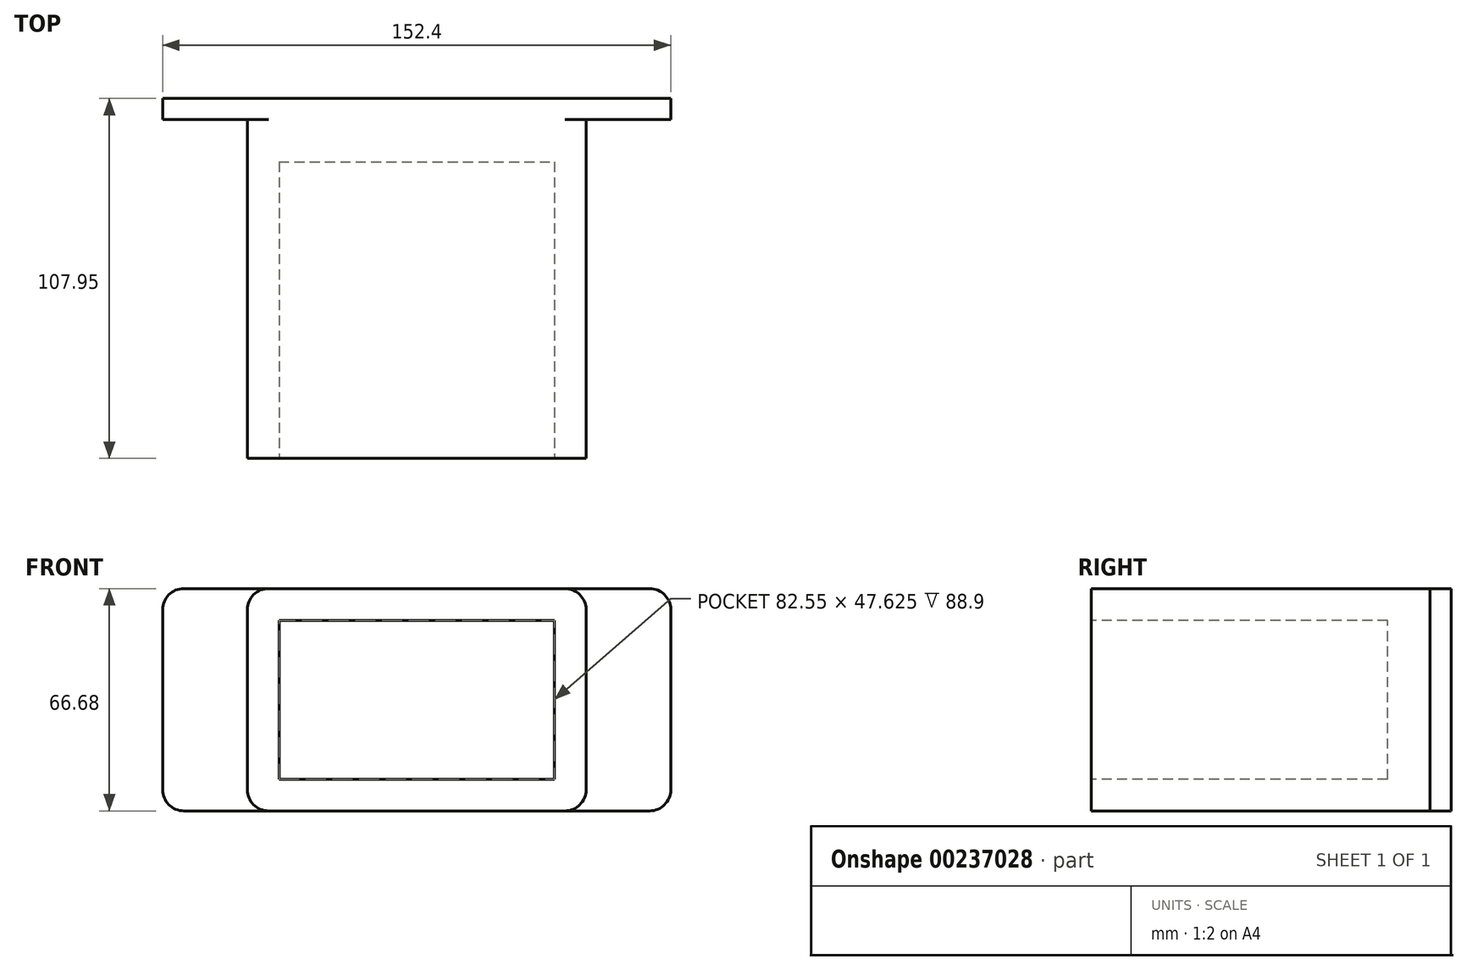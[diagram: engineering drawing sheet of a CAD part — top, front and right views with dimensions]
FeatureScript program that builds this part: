
annotation { "Feature Type Name" : "Feature", "Feature Type Description" : "" }
export const myFeature = defineFeature(function(context is Context, id is Id, definition is map)
    precondition{}
    {
        {
            var Q0;
            Q0=qCreatedBy(makeId("Front.planeOp"),FACE);
            var sketch = newSketch(context, id + "F0", { "sketchPlane" : qUnion([Q0])});
            skLineSegment(sketch, "E0.bottom", {"start": v(-76.2, -33.34) * mm, "end": v(76.2, -33.34) * mm});
            skLineSegment(sketch, "E0.top", {"start": v(-76.2, 33.34) * mm, "end": v(76.2, 33.34) * mm});
            skLineSegment(sketch, "E0.left", {"start": v(-76.2, -33.34) * mm, "end": v(-76.2, 33.34) * mm});
            skLineSegment(sketch, "E0.right", {"start": v(76.2, -33.34) * mm, "end": v(76.2, 33.34) * mm});
            skPoint(sketch, "E0.middle", {"position": v(0, 0) * mm});
            skSolve(sketch);
        }
        {
            var Q0;
            Q0 = qSketchRegion(id + "F0", true);
            extrude(context, id + "F1", {"entities" : qUnion([Q0]), "oppositeDirection" : true, "depth" : 6.35 * mm});
        }
        {
            var Q0;
            Q0=makeQuery(id+"F1.opExtrude","CAP_FACE",FACE,{"disambiguationData":[OSD([sQuery(id+"F0.wireOp",EDGE,"E0.bottom"),sQuery(id+"F0.wireOp",EDGE,"E0.top"),sQuery(id+"F0.wireOp",EDGE,"E0.left"),sQuery(id+"F0.wireOp",EDGE,"E0.right")])],"isStart":true});
            var sketch = newSketch(context, id + "F2", { "sketchPlane" : qUnion([Q0])});
            skLineSegment(sketch, "E1.bottom", {"start": v(50.8, 33.34) * mm, "end": v(-50.8, 33.34) * mm});
            skLineSegment(sketch, "E1.top", {"start": v(50.8, -33.34) * mm, "end": v(-50.8, -33.34) * mm});
            skLineSegment(sketch, "E1.left", {"start": v(50.8, 33.34) * mm, "end": v(50.8, -33.34) * mm});
            skLineSegment(sketch, "E1.right", {"start": v(-50.8, 33.34) * mm, "end": v(-50.8, -33.34) * mm});
            skPoint(sketch, "E1.middle", {"position": v(0, 0) * mm});
            skSolve(sketch);
        }
        {
            var Q0;
            Q0 = qSketchRegion(id + "F2", true);
            extrude(context, id + "F3", {"entities" : qUnion([Q0]), "operationType" : NewBodyOperationType.ADD, "depth" : 101.6 * mm});
        }
        {
            var Q0;
            Q0=makeQuery(id+"F1.opExtrude","SWEPT_EDGE",EDGE,{"disambiguationData":[OSD([sQuery(id+"F0.wireOp",EDGE,"E0.top"),sQuery(id+"F0.wireOp",EDGE,"E0.right")])]});
            var Q1;
            Q1=makeQuery(id+"F1.opExtrude","SWEPT_EDGE",EDGE,{"disambiguationData":[OSD([sQuery(id+"F0.wireOp",EDGE,"E0.bottom"),sQuery(id+"F0.wireOp",EDGE,"E0.right")])]});
            var Q2;
            Q2=makeQuery(id+"F3.opExtrude","SWEPT_EDGE",EDGE,{"disambiguationData":[OSD([sQuery(id+"F0.wireOp",EDGE,"E0.top"),sQuery(id+"F2.wireOp",EDGE,"E1.bottom"),sQuery(id+"F2.wireOp",EDGE,"E1.left")])]});
            var Q3;
            Q3=makeQuery(id+"F3.opExtrude","SWEPT_EDGE",EDGE,{"disambiguationData":[OSD([sQuery(id+"F0.wireOp",EDGE,"E0.bottom"),sQuery(id+"F2.wireOp",EDGE,"E1.top"),sQuery(id+"F2.wireOp",EDGE,"E1.left")])]});
            var Q4;
            Q4=makeQuery(id+"F1.opExtrude","SWEPT_EDGE",EDGE,{"disambiguationData":[OSD([sQuery(id+"F0.wireOp",EDGE,"E0.top"),sQuery(id+"F0.wireOp",EDGE,"E0.left")])]});
            var Q5;
            Q5=makeQuery(id+"F1.opExtrude","SWEPT_EDGE",EDGE,{"disambiguationData":[OSD([sQuery(id+"F0.wireOp",EDGE,"E0.bottom"),sQuery(id+"F0.wireOp",EDGE,"E0.left")])]});
            var Q6;
            Q6=makeQuery(id+"F3.opExtrude","SWEPT_EDGE",EDGE,{"disambiguationData":[OSD([sQuery(id+"F0.wireOp",EDGE,"E0.top"),sQuery(id+"F2.wireOp",EDGE,"E1.bottom"),sQuery(id+"F2.wireOp",EDGE,"E1.right")])]});
            var Q7;
            Q7=makeQuery(id+"F3.opExtrude","SWEPT_EDGE",EDGE,{"disambiguationData":[OSD([sQuery(id+"F0.wireOp",EDGE,"E0.bottom"),sQuery(id+"F2.wireOp",EDGE,"E1.top"),sQuery(id+"F2.wireOp",EDGE,"E1.right")])]});
            fillet(context, id + "F4", {"entities" : qUnion([Q0, Q1, Q2, Q3, Q4, Q5, Q6, Q7]), "radius" : 6.35 * mm, "tangentPropagation" : true, "allowEdgeOverflow" : false});
        }
        {
            var Q0;
            Q0=makeQuery(id+"F3.opExtrude","CAP_FACE",FACE,{"disambiguationData":[OSD([sQuery(id+"F2.wireOp",EDGE,"E1.bottom"),sQuery(id+"F2.wireOp",EDGE,"E1.top"),sQuery(id+"F2.wireOp",EDGE,"E1.left"),sQuery(id+"F2.wireOp",EDGE,"E1.right")])],"isStart":false});
            var sketch = newSketch(context, id + "F5", { "sketchPlane" : qUnion([Q0])});
            skLineSegment(sketch, "E2.bottom", {"start": v(-41.27, -23.81) * mm, "end": v(41.27, -23.81) * mm});
            skLineSegment(sketch, "E2.top", {"start": v(-41.27, 23.81) * mm, "end": v(41.27, 23.81) * mm});
            skLineSegment(sketch, "E2.left", {"start": v(-41.27, -23.81) * mm, "end": v(-41.27, 23.81) * mm});
            skLineSegment(sketch, "E2.right", {"start": v(41.27, -23.81) * mm, "end": v(41.27, 23.81) * mm});
            skPoint(sketch, "E2.middle", {"position": v(0, 0) * mm});
            skSolve(sketch);
        }
        {
            var Q0;
            Q0 = qSketchRegion(id + "F5", true);
            extrude(context, id + "F6", {"entities" : qUnion([Q0]), "operationType" : NewBodyOperationType.REMOVE, "oppositeDirection" : true, "depth" : 88.9 * mm});
        }
    });
